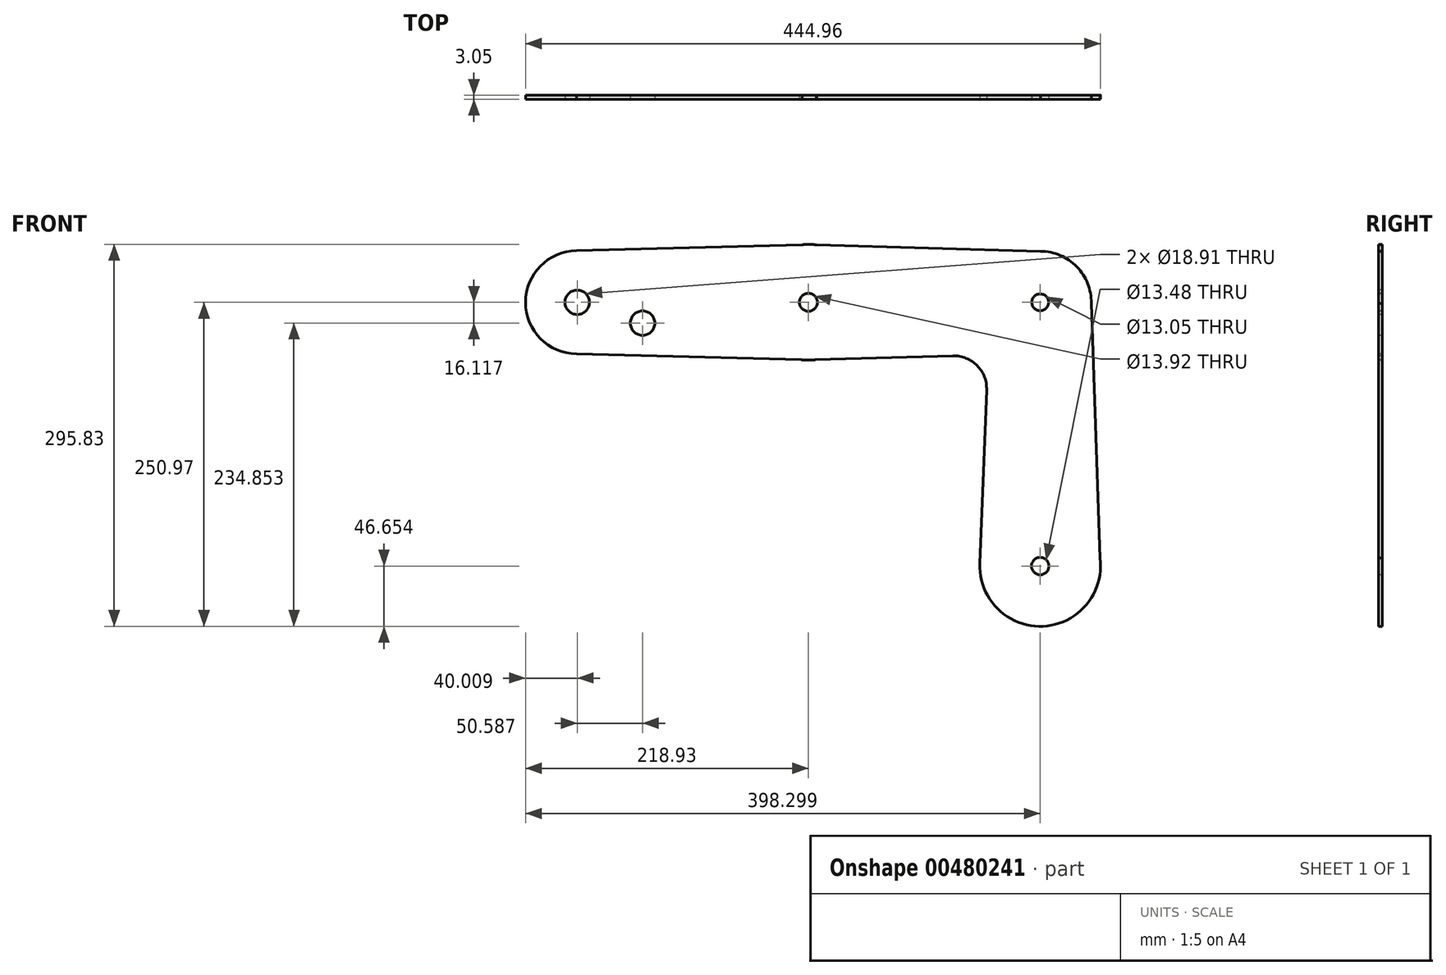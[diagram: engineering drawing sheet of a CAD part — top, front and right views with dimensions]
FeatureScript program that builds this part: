
annotation { "Feature Type Name" : "Feature", "Feature Type Description" : "" }
export const myFeature = defineFeature(function(context is Context, id is Id, definition is map)
    precondition{}
    {
        {
            var Q0;
            Q0=qCreatedBy(makeId("Front.planeOp"),FACE);
            var sketch = newSketch(context, id + "F0", { "sketchPlane" : qUnion([Q0])});
            skLineSegment(sketch, "E0", {"start": v(-178.92, 102.2) * mm, "end": v(179.37, 102.2) * mm, "construction": true});
            skLineSegment(sketch, "E1", {"start": v(179.37, 102.2) * mm, "end": v(179.37, -102.12) * mm, "construction": true});
            skCircle(sketch, "E2", {"center": v(-178.92, 102.2) * mm, "radius": 40.01 * mm});
            skCircle(sketch, "E3", {"center": v(179.37, 102.2) * mm, "radius": 39.53 * mm});
            skCircle(sketch, "E4", {"center": v(0, 102.2) * mm, "radius": 44.86 * mm});
            skCircle(sketch, "E5", {"center": v(179.37, -102.12) * mm, "radius": 46.66 * mm});
            skLineSegment(sketch, "E6", {"start": v(218.89, 101.4) * mm, "end": v(225.93, -105.1) * mm});
            skLineSegment(sketch, "E7", {"start": v(132.74, -100.53) * mm, "end": v(137.91, 34.37) * mm});
            skCircle(sketch, "E8", {"center": v(-178.92, 102.2) * mm, "radius": 9.46 * mm});
            skCircle(sketch, "E9", {"center": v(-128.33, 86.08) * mm, "radius": 9.46 * mm});
            skCircle(sketch, "E10", {"center": v(179.37, 102.2) * mm, "radius": 6.52 * mm});
            skCircle(sketch, "E11", {"center": v(179.37, -102.12) * mm, "radius": 6.74 * mm});
            skCircle(sketch, "E12", {"center": v(0, 102.2) * mm, "radius": 6.96 * mm});
            skLineSegment(sketch, "E13", {"start": v(-179.46, 142.2) * mm, "end": v(-4.86, 146.8) * mm});
            skLineSegment(sketch, "E14", {"start": v(179.63, 141.72) * mm, "end": v(6.17, 146.63) * mm});
            skLineSegment(sketch, "E15", {"start": v(-179.4, 62.19) * mm, "end": v(-5.47, 57.68) * mm});
            skLineSegment(sketch, "E16", {"start": v(111.8, 60.73) * mm, "end": v(5.37, 57.66) * mm});
            skArc(sketch, "E17.filletArc", {"start": v(137.91, 34.37) * mm, "mid": v(130.58, 53.21) * mm, "end": v(111.8, 60.73) * mm});
            skLineSegment(sketch, "E18", {"start": v(-128.33, 86.08) * mm, "end": v(-128.33, 226.36) * mm});
            skLineSegment(sketch, "E19", {"start": v(0, 102.2) * mm, "end": v(0, 226.36) * mm});
            skSolve(sketch);
        }
        {
            var Q0;
            Q0 = qSketchRegion(id + "F0", true);
            extrude(context, id + "F1", {"entities" : qUnion([Q0]), "oppositeDirection" : true, "depth" : 3.05 * mm});
        }
    });
